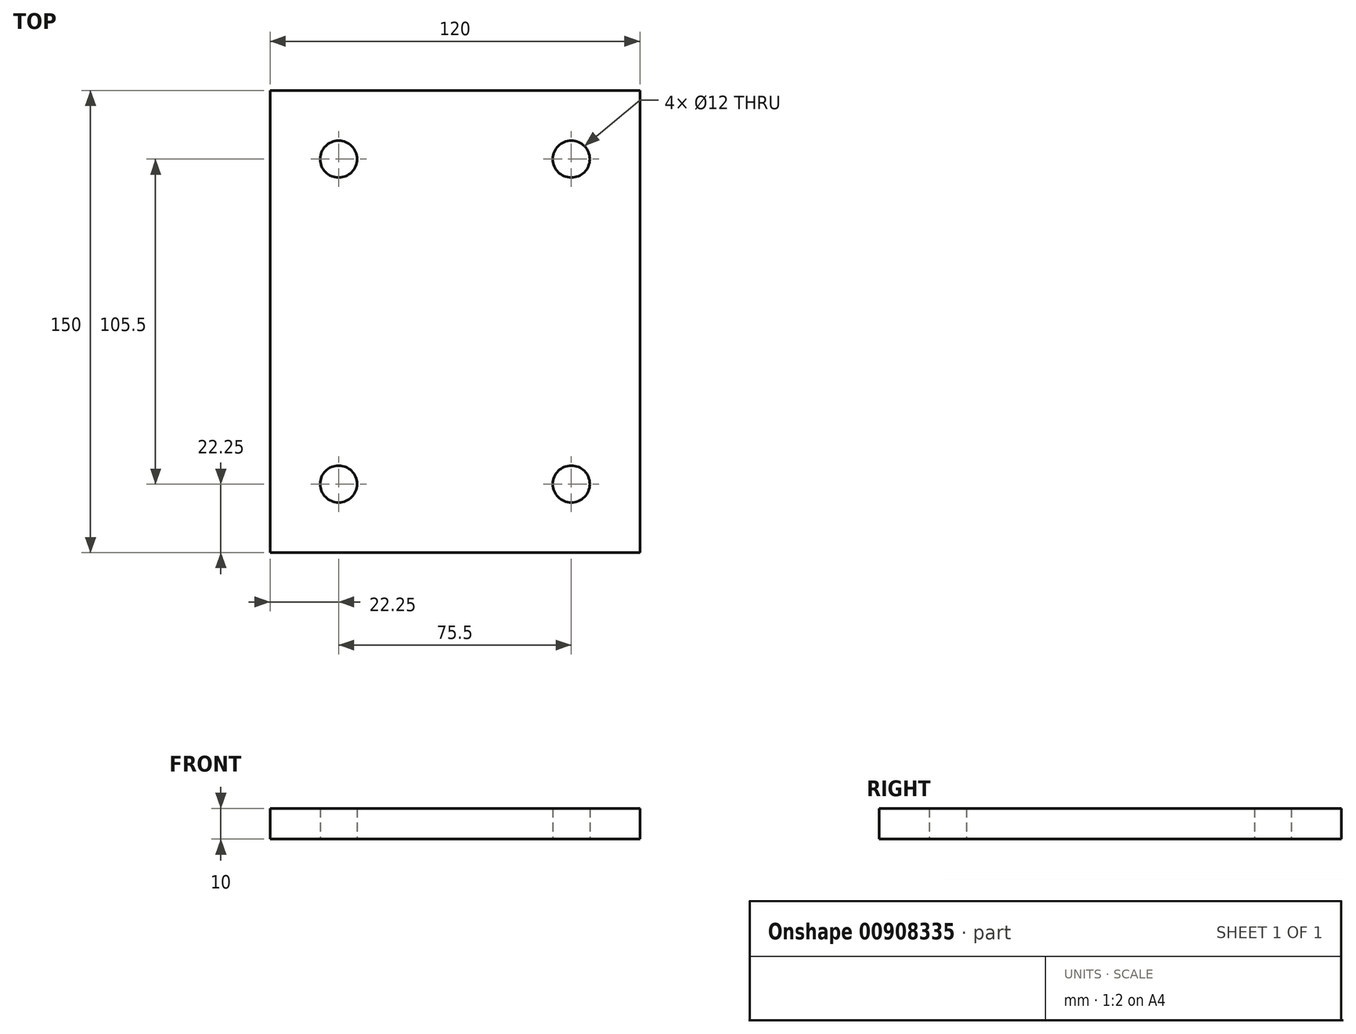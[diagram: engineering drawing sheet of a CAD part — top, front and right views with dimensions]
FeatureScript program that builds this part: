
annotation { "Feature Type Name" : "Feature", "Feature Type Description" : "" }
export const myFeature = defineFeature(function(context is Context, id is Id, definition is map)
    precondition{}
    {
        {
            var Q0;
            Q0=qCreatedBy(makeId("Top.planeOp"),FACE);
            var sketch = newSketch(context, id + "F0", { "sketchPlane" : qUnion([Q0])});
            skLineSegment(sketch, "E0.bottom", {"start": v(60, 75) * mm, "end": v(-60, 75) * mm});
            skLineSegment(sketch, "E0.top", {"start": v(60, -75) * mm, "end": v(-60, -75) * mm});
            skLineSegment(sketch, "E0.left", {"start": v(60, 75) * mm, "end": v(60, -75) * mm});
            skLineSegment(sketch, "E0.right", {"start": v(-60, 75) * mm, "end": v(-60, -75) * mm});
            skPoint(sketch, "E0.middle", {"position": v(0, 0) * mm});
            skCircle(sketch, "E1", {"center": v(-37.75, 52.75) * mm, "radius": 6 * mm});
            skCircle(sketch, "E2", {"center": v(37.75, 52.75) * mm, "radius": 6 * mm});
            skCircle(sketch, "E3", {"center": v(-37.75, -52.75) * mm, "radius": 6 * mm});
            skCircle(sketch, "E4", {"center": v(37.75, -52.75) * mm, "radius": 6 * mm});
            skSolve(sketch);
        }
        {
            var Q0;
            Q0=makeQuery(id+"F0.imprint","IMPRINT",FACE,{"disambiguationData":[TD([[makeQuery(id+"F0.imprint","IMPRINT",EDGE,{"derivedFrom":sQuery(id+"F0.wireOp",EDGE,"E0.bottom")}),1.0]])]});
            extrude(context, id + "F1", {"entities" : qUnion([Q0]), "depth" : 10 * mm, "offsetDistance" : 25 * mm});
        }
    });
